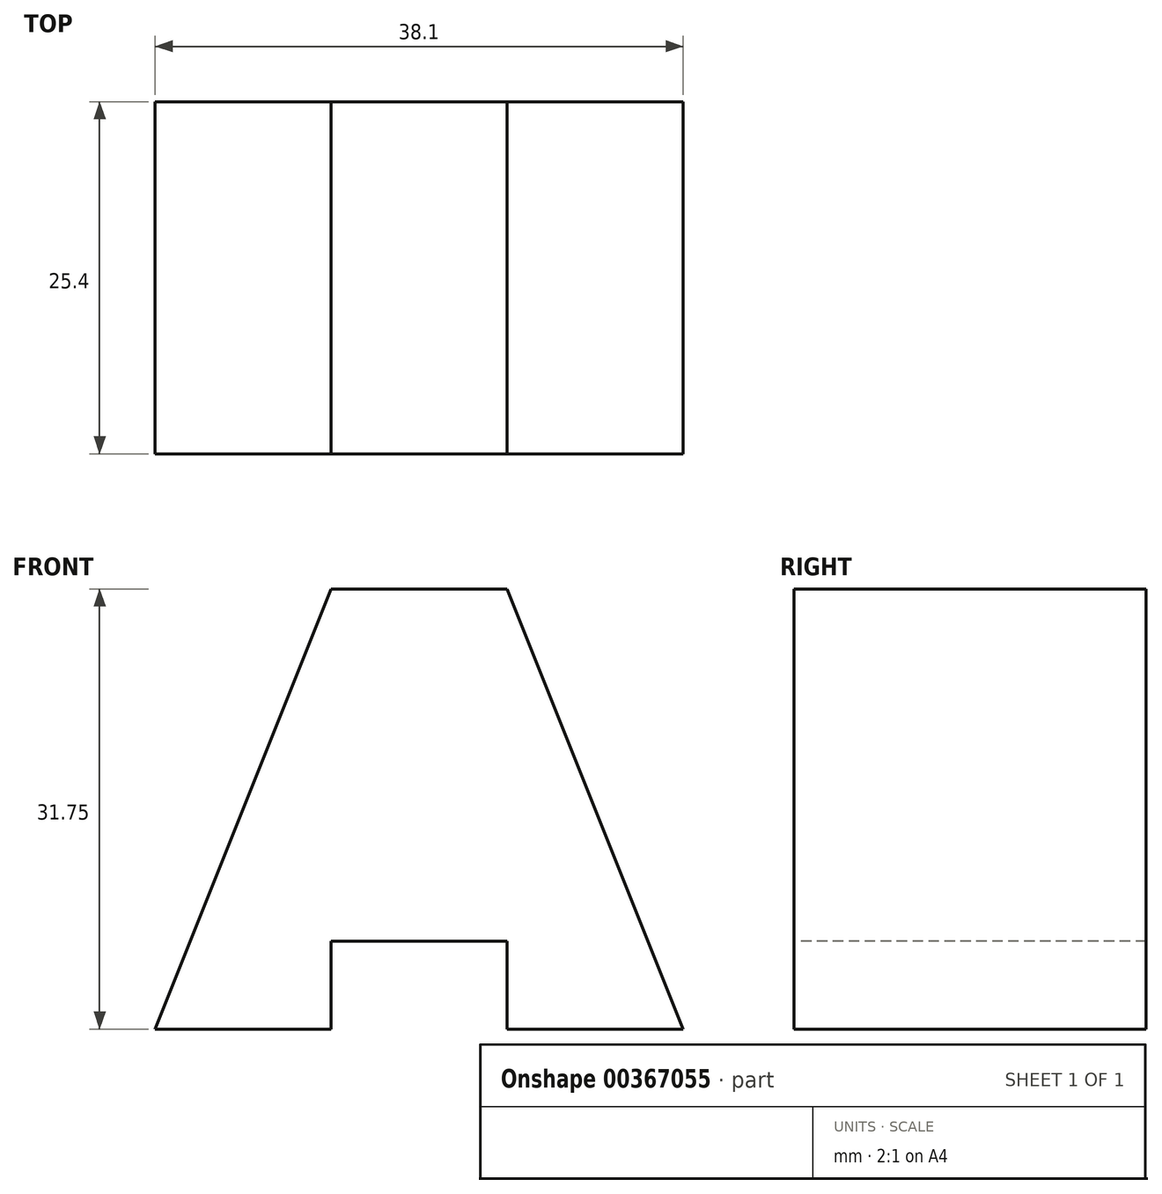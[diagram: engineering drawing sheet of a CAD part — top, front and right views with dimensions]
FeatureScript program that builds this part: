
annotation { "Feature Type Name" : "Feature", "Feature Type Description" : "" }
export const myFeature = defineFeature(function(context is Context, id is Id, definition is map)
    precondition{}
    {
        {
            var Q0;
            Q0=qCreatedBy(makeId("Front.planeOp"),FACE);
            var sketch = newSketch(context, id + "F0", { "sketchPlane" : qUnion([Q0])});
            skLineSegment(sketch, "E0", {"start": v(-46.13, 0) * mm, "end": v(-8.03, 0) * mm});
            skLineSegment(sketch, "E1", {"start": v(-8.03, 0) * mm, "end": v(-8.03, 31.75) * mm});
            skLineSegment(sketch, "E2", {"start": v(-8.03, 31.75) * mm, "end": v(-46.13, 31.75) * mm});
            skLineSegment(sketch, "E3", {"start": v(-46.13, 31.75) * mm, "end": v(-46.13, 0) * mm});
            skSolve(sketch);
        }
        {
            var Q0;
            Q0=makeQuery(id+"F0.imprint","IMPRINT",FACE,{"disambiguationData":[TD([[makeQuery(id+"F0.imprint","IMPRINT",EDGE,{"derivedFrom":sQuery(id+"F0.wireOp",EDGE,"E0")}),1.0]])]});
            extrude(context, id + "F1", {"entities" : qUnion([Q0]), "depth" : 25.4 * mm});
        }
        {
            var Q0;
            Q0=makeQuery(id+"F1.opExtrude","CAP_FACE",FACE,{"disambiguationData":[OSD([sQuery(id+"F0.wireOp",EDGE,"E0"),sQuery(id+"F0.wireOp",EDGE,"E1"),sQuery(id+"F0.wireOp",EDGE,"E2"),sQuery(id+"F0.wireOp",EDGE,"E3")])],"isStart":false});
            var sketch = newSketch(context, id + "F2", { "sketchPlane" : qUnion([Q0])});
            skLineSegment(sketch, "E4", {"start": v(-8.03, 0) * mm, "end": v(-20.73, 31.75) * mm});
            skLineSegment(sketch, "E5", {"start": v(-20.73, 31.75) * mm, "end": v(-8.03, 31.75) * mm});
            skLineSegment(sketch, "E6", {"start": v(-8.03, 31.75) * mm, "end": v(-8.03, 0) * mm});
            skLineSegment(sketch, "E7", {"start": v(-46.13, 0) * mm, "end": v(-33.43, 31.75) * mm});
            skLineSegment(sketch, "E8", {"start": v(-33.43, 31.75) * mm, "end": v(-46.13, 31.75) * mm});
            skLineSegment(sketch, "E9", {"start": v(-46.13, 31.75) * mm, "end": v(-46.13, 0) * mm});
            skLineSegment(sketch, "E10", {"start": v(-33.43, 0) * mm, "end": v(-33.43, 6.35) * mm});
            skLineSegment(sketch, "E11", {"start": v(-33.43, 6.35) * mm, "end": v(-20.73, 6.35) * mm});
            skLineSegment(sketch, "E12", {"start": v(-20.73, 6.35) * mm, "end": v(-20.73, 0) * mm});
            skLineSegment(sketch, "E13", {"start": v(-33.43, 0) * mm, "end": v(-20.73, 0) * mm});
            skSolve(sketch);
        }
        {
            var Q0;
            Q0=makeQuery(id+"F2.imprint","IMPRINT",FACE,{"disambiguationData":[TD([[makeQuery(id+"F2.imprint","IMPRINT",EDGE,{"derivedFrom":sQuery(id+"F2.wireOp",EDGE,"E7")}),1.0]])]});
            var Q1;
            Q1=makeQuery(id+"F2.imprint","IMPRINT",FACE,{"disambiguationData":[TD([[makeQuery(id+"F2.imprint","IMPRINT",EDGE,{"derivedFrom":sQuery(id+"F2.wireOp",EDGE,"E4")}),-1.0]])]});
            var Q2;
            Q2=makeQuery(id+"F2.imprint","IMPRINT",FACE,{"disambiguationData":[TD([[makeQuery(id+"F2.imprint","IMPRINT",EDGE,{"derivedFrom":sQuery(id+"F2.wireOp",EDGE,"E10")}),-1.0]])]});
            extrude(context, id + "F3", {"entities" : qUnion([Q0, Q1, Q2]), "operationType" : NewBodyOperationType.REMOVE, "oppositeDirection" : true, "depth" : 25.4 * mm});
        }
    });
